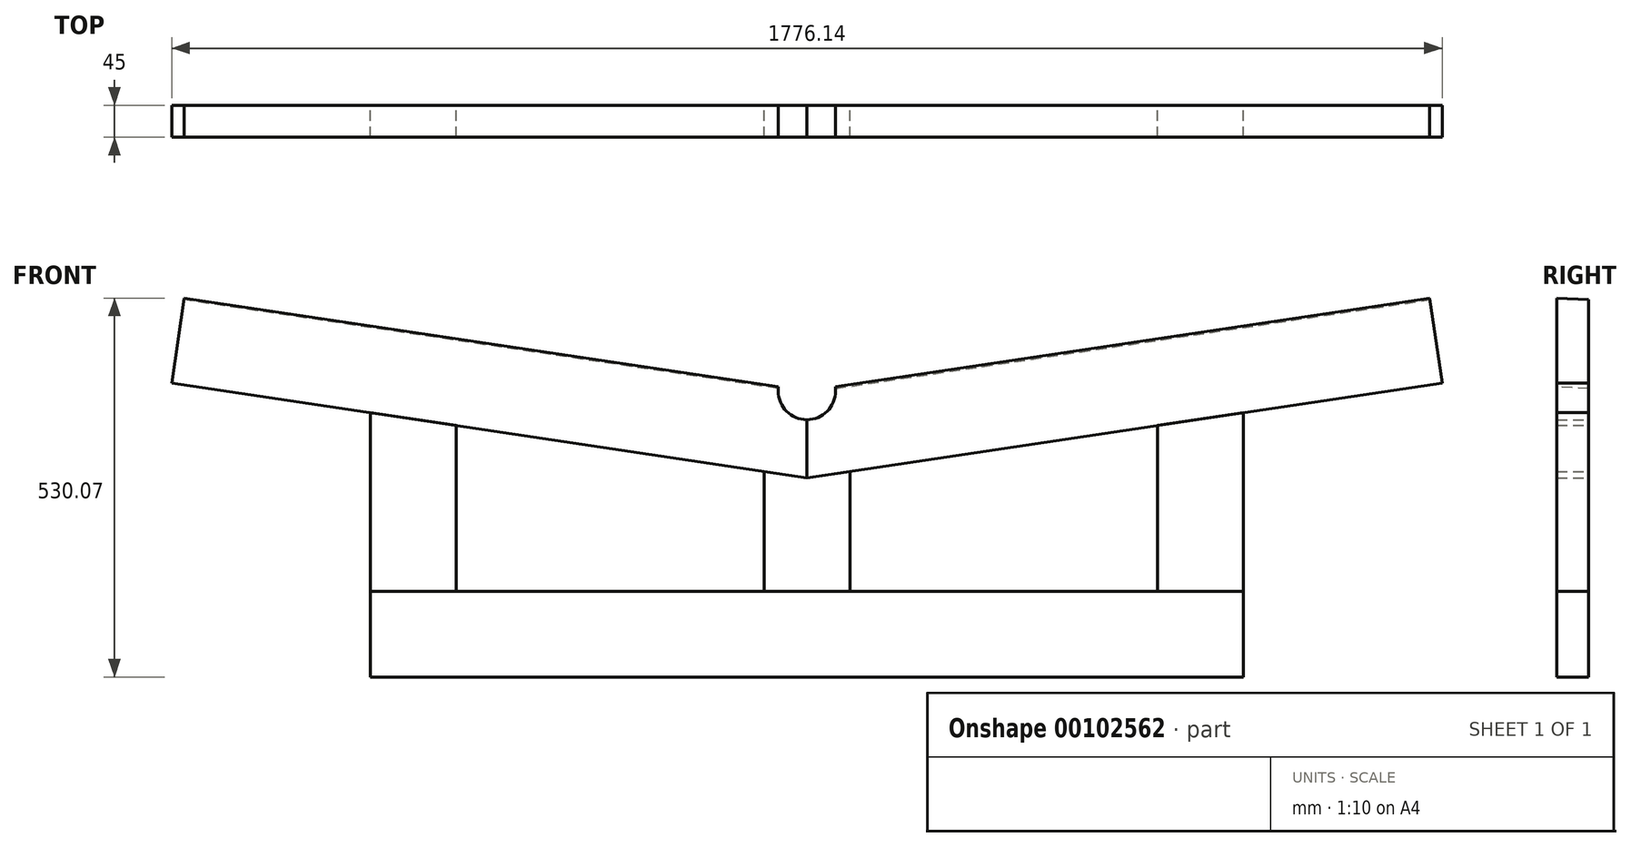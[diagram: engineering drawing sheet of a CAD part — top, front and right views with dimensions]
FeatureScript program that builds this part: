
annotation { "Feature Type Name" : "Feature", "Feature Type Description" : "" }
export const myFeature = defineFeature(function(context is Context, id is Id, definition is map)
    precondition{}
    {
        {
            var Q0;
            Q0=qCreatedBy(makeId("Front.planeOp"),FACE);
            var sketch = newSketch(context, id + "F0", { "sketchPlane" : qUnion([Q0])});
            skLineSegment(sketch, "E0.bottom", {"start": v(0, 0) * mm, "end": v(1220, 0) * mm});
            skLineSegment(sketch, "E0.top", {"start": v(0, 120) * mm, "end": v(1220, 120) * mm});
            skLineSegment(sketch, "E0.left", {"start": v(0, 0) * mm, "end": v(0, 120) * mm});
            skLineSegment(sketch, "E0.right", {"start": v(1220, 0) * mm, "end": v(1220, 120) * mm});
            skSolve(sketch);
        }
        {
            var Q0;
            Q0=qSketchRegion(id+"F0",true);
            extrude(context, id + "F1", {"entities" : qUnion([Q0]), "depth" : 45 * mm});
        }
        {
            var Q0;
            Q0=qCreatedBy(makeId("Front.planeOp"),FACE);
            var sketch = newSketch(context, id + "F2", { "sketchPlane" : qUnion([Q0])});
            skLineSegment(sketch, "E1", {"start": v(610, 0) * mm, "end": v(610, 400) * mm, "construction": true});
            skLineSegment(sketch, "E2", {"start": v(570, 405.98) * mm, "end": v(-260.33, 530.07) * mm});
            skLineSegment(sketch, "E3.0", {"start": v(610, 278.67) * mm, "end": v(-278.07, 411.4) * mm});
            skLineSegment(sketch, "E4", {"start": v(-260.33, 530.07) * mm, "end": v(-278.07, 411.4) * mm});
            skLineSegment(sketch, "E5", {"start": v(610, 278.67) * mm, "end": v(610, 360) * mm});
            skArc(sketch, "E6", {"start": v(570, 400) * mm, "mid": v(581.72, 371.72) * mm, "end": v(610, 360) * mm});
            skLineSegment(sketch, "E7", {"start": v(570, 400) * mm, "end": v(570, 405.98) * mm});
            skSolve(sketch);
        }
        {
            var Q0;
            Q0=qSketchRegion(id+"F2",true);
            extrude(context, id + "F3", {"entities" : qUnion([Q0]), "depth" : 45 * mm});
        }
        {
            var Q0;
            Q0=makeQuery(id+"F3.opExtrude","SWEPT_FACE",FACE,{"disambiguationData":[OSD([sQuery(id+"F2.wireOp",EDGE,"E4")])]});
            var sketch = newSketch(context, id + "F4", { "sketchPlane" : qUnion([Q0])});
            skLineSegment(sketch, "E8", {"start": v(0, 485.77) * mm, "end": v(45, 485.77) * mm});
            skLineSegment(sketch, "E9", {"start": v(0, 485.77) * mm, "end": v(0, 483.41) * mm});
            skLineSegment(sketch, "E10", {"start": v(0, 483.41) * mm, "end": v(45, 485.77) * mm});
            skSolve(sketch);
        }
        {
            var Q0;
            Q0=qSketchRegion(id+"F4",true);
            extrude(context, id + "F5", {"entities" : qUnion([Q0]), "operationType" : NewBodyOperationType.REMOVE, "endBound" : BoundingType.THROUGH_ALL, "oppositeDirection" : true, "depth" : 25 * mm});
        }
        {
            var Q0;
            Q0=qCreatedBy(makeId("Front.planeOp"),FACE);
            var sketch = newSketch(context, id + "F6", { "sketchPlane" : qUnion([Q0])});
            skLineSegment(sketch, "E11", {"start": v(0, 120) * mm, "end": v(0, 369.83) * mm});
            skLineSegment(sketch, "E12.0", {"start": v(120, 120) * mm, "end": v(120, 351.9) * mm});
            skLineSegment(sketch, "E13", {"start": v(0, 369.83) * mm, "end": v(120, 351.9) * mm});
            skLineSegment(sketch, "E14", {"start": v(0, 120) * mm, "end": v(120, 120) * mm});
            skSolve(sketch);
        }
        {
            var Q0;
            Q0=qSketchRegion(id+"F6",true);
            extrude(context, id + "F7", {"entities" : qUnion([Q0]), "depth" : 45 * mm});
        }
        {
            var Q0;
            Q0=qCreatedBy(makeId("Right.planeOp"),FACE);
            cPlane(context, id + "F8", {"entities" : qUnion([Q0]), "cplaneType" : CPlaneType.OFFSET, "offset" : 610 * mm, "width" : 150 * mm, "height" : 150 * mm});
        }
        {
            var Q0;
            Q0=makeQuery(id+"F3.opExtrude","SWEPT_BODY",BODY,{"disambiguationData":[OSD([sQuery(id+"F2.wireOp",EDGE,"E2"),sQuery(id+"F2.wireOp",EDGE,"E3.0"),sQuery(id+"F2.wireOp",EDGE,"E4"),sQuery(id+"F2.wireOp",EDGE,"E5"),sQuery(id+"F2.wireOp",EDGE,"E6"),sQuery(id+"F2.wireOp",EDGE,"E7")])]});
            var Q1;
            Q1=makeQuery(id+"F7.opExtrude","SWEPT_BODY",BODY,{"disambiguationData":[OSD([sQuery(id+"F6.wireOp",EDGE,"E11"),sQuery(id+"F6.wireOp",EDGE,"E12.0"),sQuery(id+"F6.wireOp",EDGE,"E13"),sQuery(id+"F6.wireOp",EDGE,"E14")])]});
            var Q2;
            Q2=qCreatedBy(id+"F8.planeOp",FACE);
            mirror(context, id + "F9", {"entities" : qUnion([Q0, Q1]), "mirrorPlane" : qUnion([Q2])});
        }
        {
            var Q0;
            Q0=qCreatedBy(makeId("Front.planeOp"),FACE);
            var sketch = newSketch(context, id + "F10", { "sketchPlane" : qUnion([Q0])});
            skLineSegment(sketch, "E15", {"start": v(610, 120) * mm, "end": v(610, 278.67) * mm, "construction": true});
            skLineSegment(sketch, "E16.0", {"start": v(670, 120) * mm, "end": v(670, 287.63) * mm});
            skLineSegment(sketch, "E17.MirrorCS", {"start": v(550, 120) * mm, "end": v(550, 287.63) * mm});
            skLineSegment(sketch, "E18", {"start": v(550, 287.63) * mm, "end": v(610, 278.67) * mm});
            skLineSegment(sketch, "E19", {"start": v(610, 278.67) * mm, "end": v(670, 287.63) * mm});
            skLineSegment(sketch, "E20", {"start": v(550, 120) * mm, "end": v(670, 120) * mm});
            skSolve(sketch);
        }
        {
            var Q0;
            Q0=qSketchRegion(id+"F10",true);
            extrude(context, id + "F11", {"entities" : qUnion([Q0]), "depth" : 45 * mm});
        }
    });
